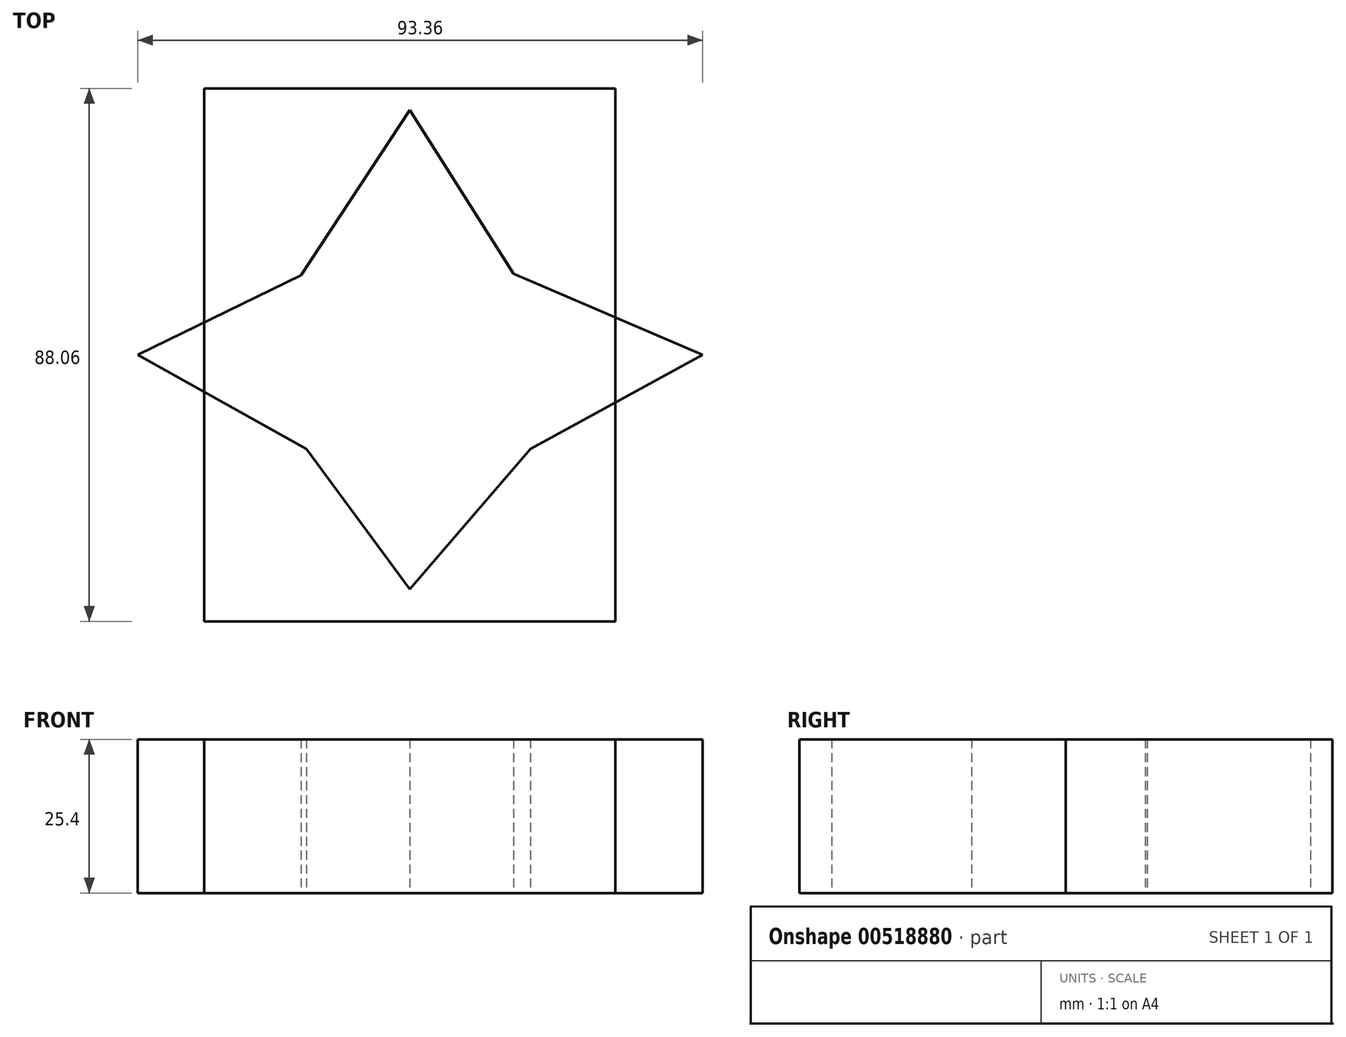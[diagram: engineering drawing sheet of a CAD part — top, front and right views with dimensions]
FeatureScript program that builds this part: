
annotation { "Feature Type Name" : "Feature", "Feature Type Description" : "" }
export const myFeature = defineFeature(function(context is Context, id is Id, definition is map)
    precondition{}
    {
        {
            var Q0;
            Q0=qCreatedBy(makeId("Top.planeOp"),FACE);
            var sketch = newSketch(context, id + "F0", { "sketchPlane" : qUnion([Q0])});
            skLineSegment(sketch, "E0.bottom", {"start": v(33.96, 44.03) * mm, "end": v(-33.96, 44.03) * mm});
            skLineSegment(sketch, "E0.top", {"start": v(33.96, -44.03) * mm, "end": v(-33.96, -44.03) * mm});
            skLineSegment(sketch, "E0.left", {"start": v(33.96, 44.03) * mm, "end": v(33.96, -44.03) * mm});
            skLineSegment(sketch, "E0.right", {"start": v(-33.96, 44.03) * mm, "end": v(-33.96, -44.03) * mm});
            skPoint(sketch, "E0.middle", {"position": v(0, 0) * mm});
            skSolve(sketch);
        }
        {
            var Q0;
            Q0=makeQuery(id+"F0.imprint","IMPRINT",FACE,{"disambiguationData":[TD([[makeQuery(id+"F0.imprint","IMPRINT",EDGE,{"derivedFrom":sQuery(id+"F0.wireOp",EDGE,"E0.bottom")}),1.0]])]});
            var sketch = newSketch(context, id + "F1", { "sketchPlane" : qUnion([Q0])});
            skLineSegment(sketch, "E1", {"start": v(-17.92, 13.14) * mm, "end": v(0, 40.45) * mm});
            skLineSegment(sketch, "E2", {"start": v(0, 40.45) * mm, "end": v(17.2, 13.41) * mm});
            skLineSegment(sketch, "E3", {"start": v(17.2, 13.41) * mm, "end": v(48.41, 0) * mm});
            skLineSegment(sketch, "E4", {"start": v(48.41, 0) * mm, "end": v(19.98, -15.57) * mm});
            skLineSegment(sketch, "E5", {"start": v(19.98, -15.57) * mm, "end": v(0, -38.7) * mm});
            skLineSegment(sketch, "E6", {"start": v(0, -38.7) * mm, "end": v(-17.08, -15.57) * mm});
            skLineSegment(sketch, "E7", {"start": v(-17.08, -15.57) * mm, "end": v(-44.95, 0) * mm});
            skLineSegment(sketch, "E8", {"start": v(-44.95, 0) * mm, "end": v(-17.92, 13.14) * mm});
            skSolve(sketch);
        }
        {
            var Q0;
            Q0 = qSketchRegion(id + "F1", true);
            extrude(context, id + "F2", {"entities" : qUnion([Q0]), "depth" : 25.4 * mm});
        }
        {
            var Q0;
            Q0=makeQuery(id+"F0.imprint","IMPRINT",FACE,{"disambiguationData":[TD([[makeQuery(id+"F0.imprint","IMPRINT",EDGE,{"derivedFrom":sQuery(id+"F0.wireOp",EDGE,"E0.bottom")}),1.0]])]});
            extrude(context, id + "F3", {"entities" : qUnion([Q0]), "depth" : 25.4 * mm});
        }
    });
